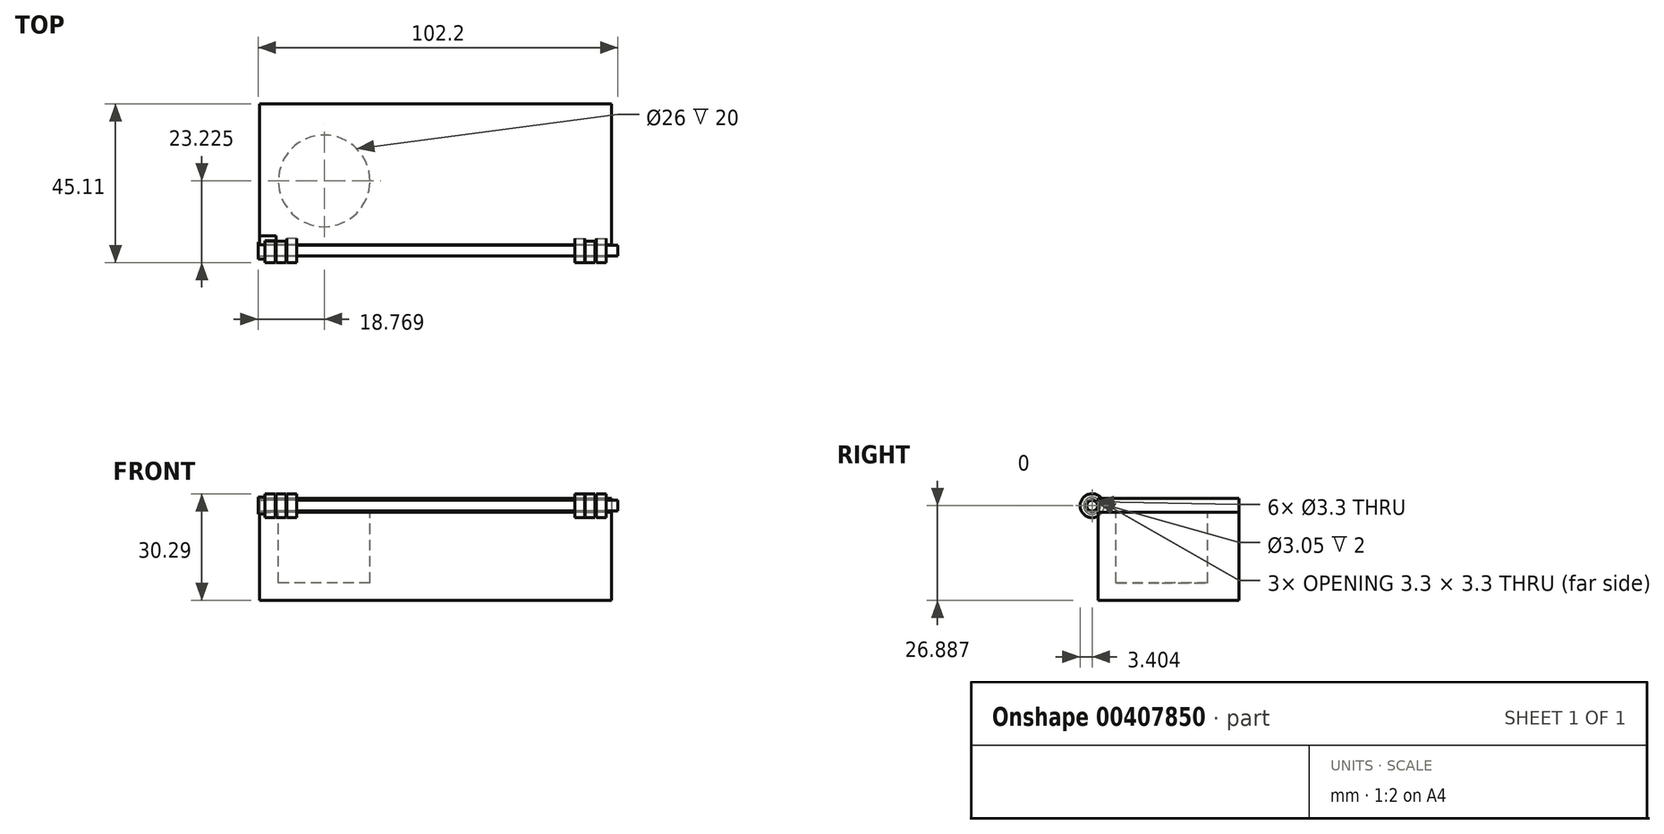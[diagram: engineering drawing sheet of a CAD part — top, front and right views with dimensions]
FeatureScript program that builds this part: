
annotation { "Feature Type Name" : "Feature", "Feature Type Description" : "" }
export const myFeature = defineFeature(function(context is Context, id is Id, definition is map)
    precondition{}
    {
        {
            var Q0;
            Q0=qCreatedBy(makeId("Top.planeOp"),FACE);
            var sketch = newSketch(context, id + "F0", { "sketchPlane" : qUnion([Q0])});
            skLineSegment(sketch, "E0.bottom", {"start": v(-51.53, 19.94) * mm, "end": v(48.47, 19.94) * mm});
            skLineSegment(sketch, "E0.top", {"start": v(-51.53, -20.06) * mm, "end": v(48.47, -20.06) * mm});
            skLineSegment(sketch, "E0.left", {"start": v(-51.53, 19.94) * mm, "end": v(-51.53, -20.06) * mm});
            skLineSegment(sketch, "E0.right", {"start": v(48.47, 19.94) * mm, "end": v(48.47, -20.06) * mm});
            skSolve(sketch);
        }
        {
            var Q0;
            Q0 = qSketchRegion(id + "F0", true);
            extrude(context, id + "F1", {"entities" : qUnion([Q0]), "oppositeDirection" : true, "depth" : 25 * mm});
        }
        {
            var Q0;
            Q0=makeQuery(id+"F1.opExtrude","CAP_FACE",FACE,{"disambiguationData":[OSD([sQuery(id+"F0.wireOp",EDGE,"E0.bottom"),sQuery(id+"F0.wireOp",EDGE,"E0.top"),sQuery(id+"F0.wireOp",EDGE,"E0.left"),sQuery(id+"F0.wireOp",EDGE,"E0.right")])],"isStart":true});
            var sketch = newSketch(context, id + "F2", { "sketchPlane" : qUnion([Q0])});
            skCircle(sketch, "E1", {"center": v(-33.16, -1.95) * mm, "radius": 13 * mm});
            skSolve(sketch);
        }
        {
            var Q0;
            Q0=makeQuery(id+"F2.imprint","IMPRINT",FACE,{"disambiguationData":[TD([[makeQuery(id+"F2.imprint","IMPRINT",EDGE,{"derivedFrom":sQuery(id+"F2.wireOp",EDGE,"E1")}),1.0]])]});
            extrude(context, id + "F3", {"entities" : qUnion([Q0]), "operationType" : NewBodyOperationType.REMOVE, "oppositeDirection" : true, "depth" : 20 * mm});
        }
        {
            var Q0;
            Q0=makeQuery(id+"F1.opExtrude","SWEPT_BODY",BODY,{"disambiguationData":[OSD([sQuery(id+"F0.wireOp",EDGE,"E0.bottom"),sQuery(id+"F0.wireOp",EDGE,"E0.top"),sQuery(id+"F0.wireOp",EDGE,"E0.left"),sQuery(id+"F0.wireOp",EDGE,"E0.right")])]});
            var Q1;
            Q1=makeQuery(id+"F1.opExtrude","CAP_VERTEX",VERTEX,{"disambiguationData":[OSD([sQuery(id+"F0.wireOp",EDGE,"E0.bottom"),sQuery(id+"F0.wireOp",EDGE,"E0.right")])],"isStart":true});
            var Q2;
            Q2=qCreatedBy(makeId("Origin.pointOp"),VERTEX);
            transform(context, id + "F4", {"entities" : qUnion([Q0]), "transformType" : TransformType.TRANSLATION_ENTITY, "oppositeDirectionEntity" : false, "transformLine" : qUnion([Q1, Q2]), "makeCopy" : false});
        }
        {
            var Q0;
            Q0=makeQuery(id+"F1.opExtrude","CAP_EDGE",EDGE,{"disambiguationData":[OSD([sQuery(id+"F0.wireOp",EDGE,"E0.right")])],"isStart":true});
            cPoint(context, id + "F5", {"entities" : qUnion([Q0]), "parameter" : 0.5});
        }
        {
            var Q0;
            Q0=makeQuery(id+"F1.opExtrude","SWEPT_BODY",BODY,{"disambiguationData":[OSD([sQuery(id+"F0.wireOp",EDGE,"E0.bottom"),sQuery(id+"F0.wireOp",EDGE,"E0.top"),sQuery(id+"F0.wireOp",EDGE,"E0.left"),sQuery(id+"F0.wireOp",EDGE,"E0.right")])]});
            var Q1;
            Q1=makeQuery(id+"F1.opExtrude","CAP_VERTEX",VERTEX,{"disambiguationData":[OSD([sQuery(id+"F0.wireOp",EDGE,"E0.top"),sQuery(id+"F0.wireOp",EDGE,"E0.right")])],"isStart":true});
            var Q2;
            Q2 = qCreatedBy(id + "F5" ,VERTEX);
            transform(context, id + "F6", {"entities" : qUnion([Q0]), "transformType" : TransformType.TRANSLATION_ENTITY, "oppositeDirectionEntity" : false, "transformLine" : qUnion([Q1, Q2]), "makeCopy" : false});
        }
        {
            var Q0;
            Q0=makeQuery(id+"F1.opExtrude","CAP_EDGE",EDGE,{"disambiguationData":[OSD([sQuery(id+"F0.wireOp",EDGE,"E0.bottom")])],"isStart":true});
            cPoint(context, id + "F7", {"entities" : qUnion([Q0]), "parameter" : 0.5});
        }
        {
            var Q0;
            Q0=makeQuery(id+"F1.opExtrude","SWEPT_BODY",BODY,{"disambiguationData":[OSD([sQuery(id+"F0.wireOp",EDGE,"E0.bottom"),sQuery(id+"F0.wireOp",EDGE,"E0.top"),sQuery(id+"F0.wireOp",EDGE,"E0.left"),sQuery(id+"F0.wireOp",EDGE,"E0.right")])]});
            var Q1;
            Q1=makeQuery(id+"F1.opExtrude","CAP_VERTEX",VERTEX,{"disambiguationData":[OSD([sQuery(id+"F0.wireOp",EDGE,"E0.bottom"),sQuery(id+"F0.wireOp",EDGE,"E0.left")])],"isStart":true});
            var Q2;
            Q2 = qCreatedBy(id + "F7" ,VERTEX);
            transform(context, id + "F8", {"entities" : qUnion([Q0]), "transformType" : TransformType.TRANSLATION_ENTITY, "oppositeDirectionEntity" : false, "transformLine" : qUnion([Q1, Q2]), "makeCopy" : false});
        }
        {
            var Q0;
            Q0=qCreatedBy(makeId("Right.planeOp"),FACE);
            var sketch = newSketch(context, id + "F9", { "sketchPlane" : qUnion([Q0])});
            skCircle(sketch, "E2", {"center": v(-29.94, 24.74) * mm, "radius": 3.4 * mm});
            skSolve(sketch);
        }
        {
            var Q0;
            Q0=makeQuery(id+"F9.imprint","IMPRINT",FACE,{"disambiguationData":[TD([[makeQuery(id+"F9.imprint","IMPRINT",EDGE,{"derivedFrom":sQuery(id+"F9.wireOp",EDGE,"E2")}),1.0]])]});
            extrude(context, id + "F10", {"entities" : qUnion([Q0]), "depth" : 2.8 * mm});
        }
        {
            var Q0;
            Q0=makeQuery(id+"F10.opExtrude","CAP_FACE",FACE,{"disambiguationData":[OSD([sQuery(id+"F9.wireOp",EDGE,"E2")])],"isStart":true});
            var sketch = newSketch(context, id + "F11", { "sketchPlane" : qUnion([Q0])});
            skCircle(sketch, "E3.0", {"center": v(29.94, 24.74) * mm, "radius": 1.65 * mm});
            skSolve(sketch);
        }
        {
            var Q0;
            Q0=makeQuery(id+"F11.imprint","IMPRINT",FACE,{"disambiguationData":[TD([[makeQuery(id+"F11.imprint","IMPRINT",EDGE,{"derivedFrom":sQuery(id+"F11.wireOp",EDGE,"E3.0")}),1.0]])]});
            extrude(context, id + "F12", {"entities" : qUnion([Q0]), "operationType" : NewBodyOperationType.REMOVE, "oppositeDirection" : true, "depth" : 25 * mm});
        }
        {
            var Q0;
            Q0=qCreatedBy(makeId("Right.planeOp"),FACE);
            var sketch = newSketch(context, id + "F13", { "sketchPlane" : qUnion([Q0])});
            skPoint(sketch, "E4", {"position": v(-30, 24.73) * mm});
            skPoint(sketch, "E5", {"position": v(-28.23, 22.85) * mm});
            skSolve(sketch);
        }
        {
            var Q0;
            Q0=makeQuery(id+"F10.opExtrude","SWEPT_BODY",BODY,{"disambiguationData":[OSD([sQuery(id+"F9.wireOp",EDGE,"E2")])]});
            var Q1;
            Q1=sQuery(id+"F13.wireOp",VERTEX,"E5");
            var Q2;
            Q2=makeQuery(id+"F1.opExtrude","CAP_VERTEX",VERTEX,{"disambiguationData":[OSD([sQuery(id+"F0.wireOp",EDGE,"E0.top"),sQuery(id+"F0.wireOp",EDGE,"E0.left")])],"isStart":true});
            transform(context, id + "F14", {"entities" : qUnion([Q0]), "transformType" : TransformType.TRANSLATION_ENTITY, "oppositeDirectionEntity" : false, "transformLine" : qUnion([Q1, Q2]), "makeCopy" : false});
        }
        {
            var Q0;
            Q0=makeQuery(id+"F10.opExtrude","SWEPT_BODY",BODY,{"disambiguationData":[OSD([sQuery(id+"F9.wireOp",EDGE,"E2")])]});
            var Q1;
            Q1=makeQuery(id+"F1.opExtrude","CAP_EDGE",EDGE,{"disambiguationData":[OSD([sQuery(id+"F0.wireOp",EDGE,"E0.top")])],"isStart":true});
            transform(context, id + "F15", {"entities" : qUnion([Q0]), "transformType" : TransformType.TRANSLATION_DISTANCE, "transformDirection" : qUnion([Q1]), "distance" : 1.6 * mm, "makeCopy" : false});
        }
        {
            var Q0;
            Q0=makeQuery(id+"F10.opExtrude","SWEPT_BODY",BODY,{"disambiguationData":[OSD([sQuery(id+"F9.wireOp",EDGE,"E2")])]});
            var Q1;
            Q1=makeQuery(id+"F1.opExtrude","CAP_EDGE",EDGE,{"disambiguationData":[OSD([sQuery(id+"F0.wireOp",EDGE,"E0.top")])],"isStart":true});
            var Q2;
            Q2=makeQuery(id+"F10.opExtrude","SWEPT_FACE",FACE,{"disambiguationData":[OSD([sQuery(id+"F9.wireOp",EDGE,"E2")])]});
            transform(context, id + "F16", {"entities" : qUnion([Q0]), "transformType" : TransformType.TRANSLATION_DISTANCE, "transformDirection" : qUnion([Q1, Q2]), "distance" : 6.1 * mm, "makeCopy" : true});
        }
        {
            var Q0;
            Q0=makeQuery(id+"F10.opExtrude","SWEPT_BODY",BODY,{"disambiguationData":[OSD([sQuery(id+"F9.wireOp",EDGE,"E2")])]});
            var Q1;
            Q1=makeQuery(id+"F16.opPattern","COPY",BODY,{"derivedFrom":makeQuery(id+"F10.opExtrude","SWEPT_BODY",BODY,{"disambiguationData":[OSD([sQuery(id+"F9.wireOp",EDGE,"E2")])]}),"instanceName":"1"});
            var Q2;
            Q2=qCreatedBy(makeId("Right.planeOp"),FACE);
            mirror(context, id + "F17", {"entities" : qUnion([Q0, Q1]), "mirrorPlane" : qUnion([Q2])});
        }
        {
            var Q0;
            Q0=makeQuery(id+"F10.opExtrude","CAP_FACE",FACE,{"disambiguationData":[OSD([sQuery(id+"F9.wireOp",EDGE,"E2")])],"isStart":true});
            var sketch = newSketch(context, id + "F18", { "sketchPlane" : qUnion([Q0])});
            skCircle(sketch, "E6", {"center": v(21.7, 1.89) * mm, "radius": 1.53 * mm});
            skSolve(sketch);
        }
        {
            var Q0;
            Q0=makeQuery(id+"F18.imprint","IMPRINT",FACE,{"disambiguationData":[TD([[makeQuery(id+"F18.imprint","IMPRINT",EDGE,{"derivedFrom":sQuery(id+"F18.wireOp",EDGE,"E6")}),1.0]])]});
            extrude(context, id + "F19", {"entities" : qUnion([Q0]), "oppositeDirection" : true, "depth" : 100.2 * mm});
        }
        {
            var Q0;
            Q0=makeQuery(id+"F19.opExtrude","CAP_FACE",FACE,{"disambiguationData":[OSD([sQuery(id+"F18.wireOp",EDGE,"E6")])],"isStart":true});
            var sketch = newSketch(context, id + "F20", { "sketchPlane" : qUnion([Q0])});
            skCircle(sketch, "E7.0", {"center": v(21.7, 1.89) * mm, "radius": 2.43 * mm});
            skSolve(sketch);
        }
        {
            var Q0;
            Q0=makeQuery(id+"F20.imprint","IMPRINT",FACE,{"disambiguationData":[TD([[makeQuery(id+"F20.imprint","IMPRINT",EDGE,{"derivedFrom":sQuery(id+"F20.wireOp",EDGE,"E7.0")}),1.0]])]});
            extrude(context, id + "F21", {"entities" : qUnion([Q0]), "depth" : 2 * mm});
        }
        {
            var Q0;
            Q0=makeQuery(id+"F19.opExtrude","CAP_FACE",FACE,{"disambiguationData":[OSD([sQuery(id+"F18.wireOp",EDGE,"E6")])],"isStart":true});
            extrude(context, id + "F22", {"entities" : qUnion([Q0]), "depth" : 2 * mm});
        }
        {
            var Q0;
            Q0=qCreatedBy(makeId("Top.planeOp"),FACE);
            var sketch = newSketch(context, id + "F23", { "sketchPlane" : qUnion([Q0])});
            skLineSegment(sketch, "E8.bottom", {"start": v(83.27, -52.73) * mm, "end": v(-16.73, -52.73) * mm});
            skLineSegment(sketch, "E8.top", {"start": v(83.27, -12.73) * mm, "end": v(-16.73, -12.73) * mm});
            skLineSegment(sketch, "E8.left", {"start": v(83.27, -52.73) * mm, "end": v(83.27, -12.73) * mm});
            skLineSegment(sketch, "E8.right", {"start": v(-16.73, -52.73) * mm, "end": v(-16.73, -12.73) * mm});
            skSolve(sketch);
        }
        {
            var Q0;
            Q0=makeQuery(id+"F23.imprint","IMPRINT",FACE,{"disambiguationData":[TD([[makeQuery(id+"F23.imprint","IMPRINT",EDGE,{"derivedFrom":sQuery(id+"F23.wireOp",EDGE,"E8.bottom")}),-1.0]])]});
            extrude(context, id + "F24", {"entities" : qUnion([Q0]), "depth" : 4 * mm});
        }
        {
            var Q0;
            Q0=makeQuery(id+"F24.opExtrude","SWEPT_BODY",BODY,{"disambiguationData":[OSD([sQuery(id+"F23.wireOp",EDGE,"E8.bottom"),sQuery(id+"F23.wireOp",EDGE,"E8.top"),sQuery(id+"F23.wireOp",EDGE,"E8.left"),sQuery(id+"F23.wireOp",EDGE,"E8.right")])]});
            var Q1;
            Q1=makeQuery(id+"F24.opExtrude","CAP_VERTEX",VERTEX,{"disambiguationData":[OSD([sQuery(id+"F23.wireOp",EDGE,"E8.bottom"),sQuery(id+"F23.wireOp",EDGE,"E8.left")])],"isStart":false});
            var Q2;
            Q2=qCreatedBy(makeId("Origin.pointOp"),VERTEX);
            transform(context, id + "F25", {"entities" : qUnion([Q0]), "transformType" : TransformType.TRANSLATION_ENTITY, "oppositeDirectionEntity" : false, "transformLine" : qUnion([Q1, Q2]), "makeCopy" : false});
        }
        {
            var Q0;
            Q0=makeQuery(id+"F24.opExtrude","CAP_EDGE",EDGE,{"disambiguationData":[OSD([sQuery(id+"F23.wireOp",EDGE,"E8.right")])],"isStart":true});
            cPoint(context, id + "F26", {"entities" : qUnion([Q0]), "parameter" : 0.5});
        }
        {
            var Q0;
            Q0=makeQuery(id+"F24.opExtrude","SWEPT_BODY",BODY,{"disambiguationData":[OSD([sQuery(id+"F23.wireOp",EDGE,"E8.bottom"),sQuery(id+"F23.wireOp",EDGE,"E8.top"),sQuery(id+"F23.wireOp",EDGE,"E8.left"),sQuery(id+"F23.wireOp",EDGE,"E8.right")])]});
            var Q1;
            Q1=makeQuery(id+"F24.opExtrude","CAP_VERTEX",VERTEX,{"disambiguationData":[OSD([sQuery(id+"F23.wireOp",EDGE,"E8.top"),sQuery(id+"F23.wireOp",EDGE,"E8.right")])],"isStart":false});
            var Q2;
            Q2 = qCreatedBy(id + "F26" ,VERTEX);
            transform(context, id + "F27", {"entities" : qUnion([Q0]), "transformType" : TransformType.TRANSLATION_ENTITY, "oppositeDirectionEntity" : false, "transformLine" : qUnion([Q1, Q2]), "makeCopy" : false});
        }
        {
            var Q0;
            Q0=makeQuery(id+"F24.opExtrude","CAP_EDGE",EDGE,{"disambiguationData":[OSD([sQuery(id+"F23.wireOp",EDGE,"E8.top")])],"isStart":false});
            cPoint(context, id + "F28", {"entities" : qUnion([Q0]), "parameter" : 0.5});
        }
        {
            var Q0;
            Q0=makeQuery(id+"F24.opExtrude","SWEPT_BODY",BODY,{"disambiguationData":[OSD([sQuery(id+"F23.wireOp",EDGE,"E8.bottom"),sQuery(id+"F23.wireOp",EDGE,"E8.top"),sQuery(id+"F23.wireOp",EDGE,"E8.left"),sQuery(id+"F23.wireOp",EDGE,"E8.right")])]});
            var Q1;
            Q1=makeQuery(id+"F24.opExtrude","CAP_VERTEX",VERTEX,{"disambiguationData":[OSD([sQuery(id+"F23.wireOp",EDGE,"E8.top"),sQuery(id+"F23.wireOp",EDGE,"E8.right")])],"isStart":false});
            var Q2;
            Q2 = qCreatedBy(id + "F28" ,VERTEX);
            transform(context, id + "F29", {"entities" : qUnion([Q0]), "transformType" : TransformType.TRANSLATION_ENTITY, "oppositeDirectionEntity" : false, "transformLine" : qUnion([Q1, Q2]), "makeCopy" : false});
        }
        {
            var Q0;
            Q0=makeQuery(id+"F24.opExtrude","CAP_EDGE",EDGE,{"disambiguationData":[OSD([sQuery(id+"F23.wireOp",EDGE,"E8.left")])],"isStart":true});
            cPoint(context, id + "F30", {"entities" : qUnion([Q0]), "parameter" : 0.5});
        }
        {
            var Q0;
            Q0=makeQuery(id+"F24.opExtrude","SWEPT_BODY",BODY,{"disambiguationData":[OSD([sQuery(id+"F23.wireOp",EDGE,"E8.bottom"),sQuery(id+"F23.wireOp",EDGE,"E8.top"),sQuery(id+"F23.wireOp",EDGE,"E8.left"),sQuery(id+"F23.wireOp",EDGE,"E8.right")])]});
            var Q1;
            Q1 = qCreatedBy(id + "F30" ,VERTEX);
            var Q2;
            Q2=makeQuery(id+"F24.opExtrude","SWEPT_EDGE",EDGE,{"disambiguationData":[OSD([sQuery(id+"F23.wireOp",EDGE,"E8.top"),sQuery(id+"F23.wireOp",EDGE,"E8.right")])]});
            transform(context, id + "F31", {"entities" : qUnion([Q0]), "transformType" : TransformType.TRANSLATION_DISTANCE, "transformDirection" : qUnion([Q2]), "distance" : 8 * mm, "oppositeDirection" : true, "makeCopy" : false});
        }
        {
            var Q0;
            Q0=makeQuery(id+"F10.opExtrude","SWEPT_BODY",BODY,{"disambiguationData":[OSD([sQuery(id+"F9.wireOp",EDGE,"E2")])]});
            var Q1;
            Q1=makeQuery(id+"F24.opExtrude","CAP_EDGE",EDGE,{"disambiguationData":[OSD([sQuery(id+"F23.wireOp",EDGE,"E8.bottom")])],"isStart":false});
            var Q2;
            Q2=makeQuery(id+"F24.opExtrude","CAP_EDGE",EDGE,{"disambiguationData":[OSD([sQuery(id+"F23.wireOp",EDGE,"E8.bottom")])],"isStart":false});
            transform(context, id + "F32", {"entities" : qUnion([Q0]), "transformType" : TransformType.TRANSLATION_DISTANCE, "transformDirection" : qUnion([Q2]), "distance" : 3.1 * mm, "oppositeDirection" : true, "makeCopy" : true});
        }
        {
            var Q0;
            Q0=makeQuery(id+"F32.opPattern","COPY",BODY,{"derivedFrom":makeQuery(id+"F10.opExtrude","SWEPT_BODY",BODY,{"disambiguationData":[OSD([sQuery(id+"F9.wireOp",EDGE,"E2")])]}),"instanceName":"1"});
            var Q1;
            Q1=qCreatedBy(makeId("Right.planeOp"),FACE);
            mirror(context, id + "F33", {"entities" : qUnion([Q0]), "mirrorPlane" : qUnion([Q1])});
        }
        {
            var Q0;
            Q0=makeQuery(id+"F24.opExtrude","SWEPT_BODY",BODY,{"disambiguationData":[OSD([sQuery(id+"F23.wireOp",EDGE,"E8.bottom"),sQuery(id+"F23.wireOp",EDGE,"E8.top"),sQuery(id+"F23.wireOp",EDGE,"E8.left"),sQuery(id+"F23.wireOp",EDGE,"E8.right")])]});
            var Q1;
            Q1=makeQuery(id+"F32.opPattern","COPY",BODY,{"derivedFrom":makeQuery(id+"F10.opExtrude","SWEPT_BODY",BODY,{"disambiguationData":[OSD([sQuery(id+"F9.wireOp",EDGE,"E2")])]}),"instanceName":"1"});
            var Q2;
            Q2=makeQuery(id+"F33.opPattern","COPY",BODY,{"derivedFrom":makeQuery(id+"F32.opPattern","COPY",BODY,{"derivedFrom":makeQuery(id+"F10.opExtrude","SWEPT_BODY",BODY,{"disambiguationData":[OSD([sQuery(id+"F9.wireOp",EDGE,"E2")])]}),"instanceName":"1"}),"instanceName":"1"});
            booleanBodies(context, id + "F34", {"operationType" : BooleanOperationType.UNION, "tools" : qUnion([Q0, Q1, Q2])});
        }
        {
            var Q0;
            {var subQ0=sQuery(id+"F23.wireOp",EDGE,"E8.right");var subQ3=sQuery(id+"F23.wireOp",EDGE,"E8.bottom");Q0=makeQuery(id+"F34.opBoolean","SPLIT",FACE,{"disambiguationData":[TD([makeQuery(id+"F24.opExtrude","SWEPT_FACE",FACE,{"disambiguationData":[OSD([subQ0])]})])],"derivedFrom":makeQuery(id+"F24.opExtrude","SWEPT_FACE",FACE,{"disambiguationData":[OSD([subQ3])]})});}
            extrude(context, id + "F35", {"entities" : qUnion([Q0]), "operationType" : NewBodyOperationType.REMOVE, "oppositeDirection" : true, "depth" : 2.5 * mm});
        }
    });
